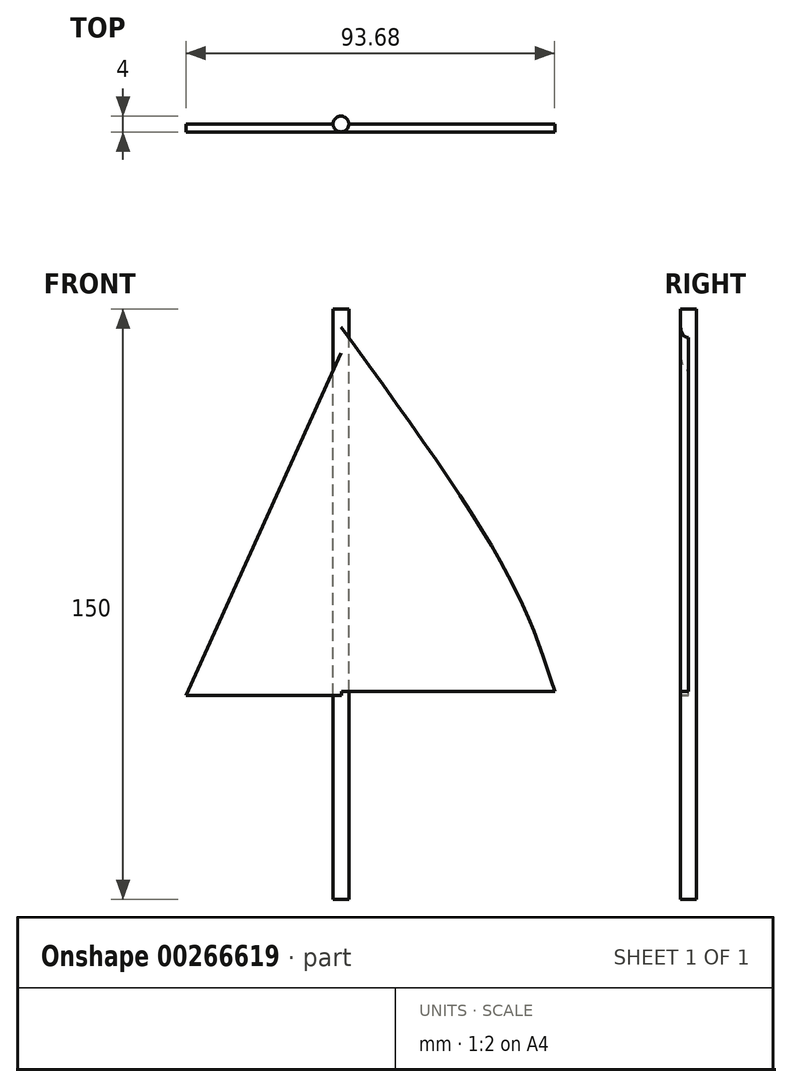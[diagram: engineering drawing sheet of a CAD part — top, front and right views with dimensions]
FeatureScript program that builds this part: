
annotation { "Feature Type Name" : "Feature", "Feature Type Description" : "" }
export const myFeature = defineFeature(function(context is Context, id is Id, definition is map)
    precondition{}
    {
        {
            var Q0;
            Q0=qCreatedBy(makeId("Front.planeOp"),FACE);
            var sketch = newSketch(context, id + "F0", { "sketchPlane" : qUnion([Q0])});
            skLineSegment(sketch, "E0", {"start": v(0, -29.25) * mm, "end": v(0, 63.38) * mm});
            skLineSegment(sketch, "E1", {"start": v(0, -29.25) * mm, "end": v(54.3, -29.25) * mm});
            skFitSpline(sketch, "E2", {"points": [v(0, 63.38) * mm, v(42.62, 0) * mm, v(54.3, -29.25) * mm], "startDerivative": vector(82.2, -113) * mm, "endDerivative": vector(22.04, -69.07) * mm});
            skSolve(sketch);
        }
        {
            var Q0;
            Q0=qCreatedBy(makeId("Front.planeOp"),FACE);
            var sketch = newSketch(context, id + "F1", { "sketchPlane" : qUnion([Q0])});
            skLineSegment(sketch, "E3.bottom", {"start": v(0, 67.94) * mm, "end": v(-2, 67.94) * mm});
            skLineSegment(sketch, "E3.top", {"start": v(0, -82.06) * mm, "end": v(-2, -82.06) * mm});
            skLineSegment(sketch, "E3.left", {"start": v(0, 67.94) * mm, "end": v(0, -82.06) * mm});
            skLineSegment(sketch, "E3.right", {"start": v(-2, 67.94) * mm, "end": v(-2, -82.06) * mm});
            skSolve(sketch);
        }
        {
            var Q0;
            Q0=qCreatedBy(makeId("Front.planeOp"),FACE);
            var sketch = newSketch(context, id + "F2", { "sketchPlane" : qUnion([Q0])});
            skLineSegment(sketch, "E4", {"start": v(0, 56.7) * mm, "end": v(-39.38, -30.21) * mm});
            skLineSegment(sketch, "E5", {"start": v(-39.38, -30.21) * mm, "end": v(0.17, -30.21) * mm});
            skLineSegment(sketch, "E6", {"start": v(0, 56.7) * mm, "end": v(0.17, -30.21) * mm});
            skSolve(sketch);
        }
        {
            var Q0;
            Q0=qCreatedBy(makeId("Front.planeOp"),FACE);
            var sketch = newSketch(context, id + "F3", { "sketchPlane" : qUnion([Q0])});
            skLineSegment(sketch, "E7", {"start": v(0, 73.3) * mm, "end": v(0, -41.11) * mm});
            skPoint(sketch, "E8", {"position": v(0, 57.45) * mm});
            skPoint(sketch, "E9", {"position": v(0, -30.21) * mm});
            skSolve(sketch);
        }
        {
            var Q0;
            Q0=makeQuery(id+"F1.imprint","IMPRINT",FACE,{"disambiguationData":[TD([[makeQuery(id+"F1.imprint","IMPRINT",EDGE,{"derivedFrom":sQuery(id+"F1.wireOp",EDGE,"E3.bottom")}),1.0]])]});
            var Q1;
            Q1=sQuery(id+"F3.wireOp",EDGE,"E7");
            revolve(context, id + "F4", {"entities" : qUnion([Q0]), "axis" : qUnion([Q1]), "revolveType" : RevolveType.FULL});
        }
        {
            var Q0;
            Q0 = qSketchRegion(id + "F0", true);
            extrude(context, id + "F5", {"entities" : qUnion([Q0]), "operationType" : NewBodyOperationType.ADD, "depth" : 2 * mm});
        }
        {
            var Q0;
            Q0=sQuery(id+"F2.wireOp",EDGE,"E4");
            var Q1;
            Q1=sQuery(id+"F2.wireOp",EDGE,"E5");
            extrude(context, id + "F6", {"bodyType" : ToolBodyType.SURFACE, "surfaceEntities" : qUnion([Q0, Q1]), "depth" : 2 * mm});
        }
        {
            var Q0;
            Q0 = qSketchRegion(id + "F2", true);
            extrude(context, id + "F7", {"entities" : qUnion([Q0]), "operationType" : NewBodyOperationType.ADD, "depth" : 2 * mm});
        }
    });
